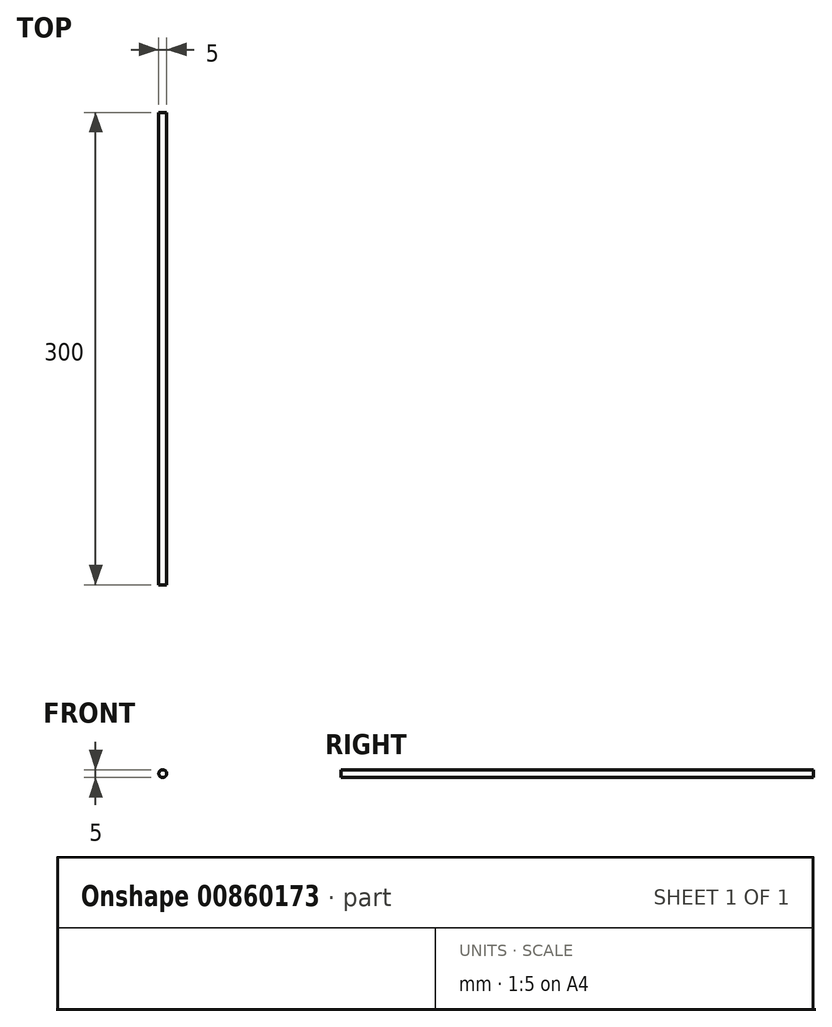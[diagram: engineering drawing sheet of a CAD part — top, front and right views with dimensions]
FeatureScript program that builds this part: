
annotation { "Feature Type Name" : "Feature", "Feature Type Description" : "" }
export const myFeature = defineFeature(function(context is Context, id is Id, definition is map)
    precondition{}
    {
        {
            var Q0;
            Q0=qCreatedBy(makeId("Front.planeOp"),FACE);
            var sketch = newSketch(context, id + "F0", { "sketchPlane" : qUnion([Q0])});
            skCircle(sketch, "E0", {"center": v(0, 0) * mm, "radius": 2.5 * mm});
            skSolve(sketch);
        }
        {
            var Q0;
            Q0 = qSketchRegion(id + "F0", true);
            extrude(context, id + "F1", {"entities" : qUnion([Q0]), "depth" : 300 * mm, "offsetDistance" : 25 * mm});
        }
    });
